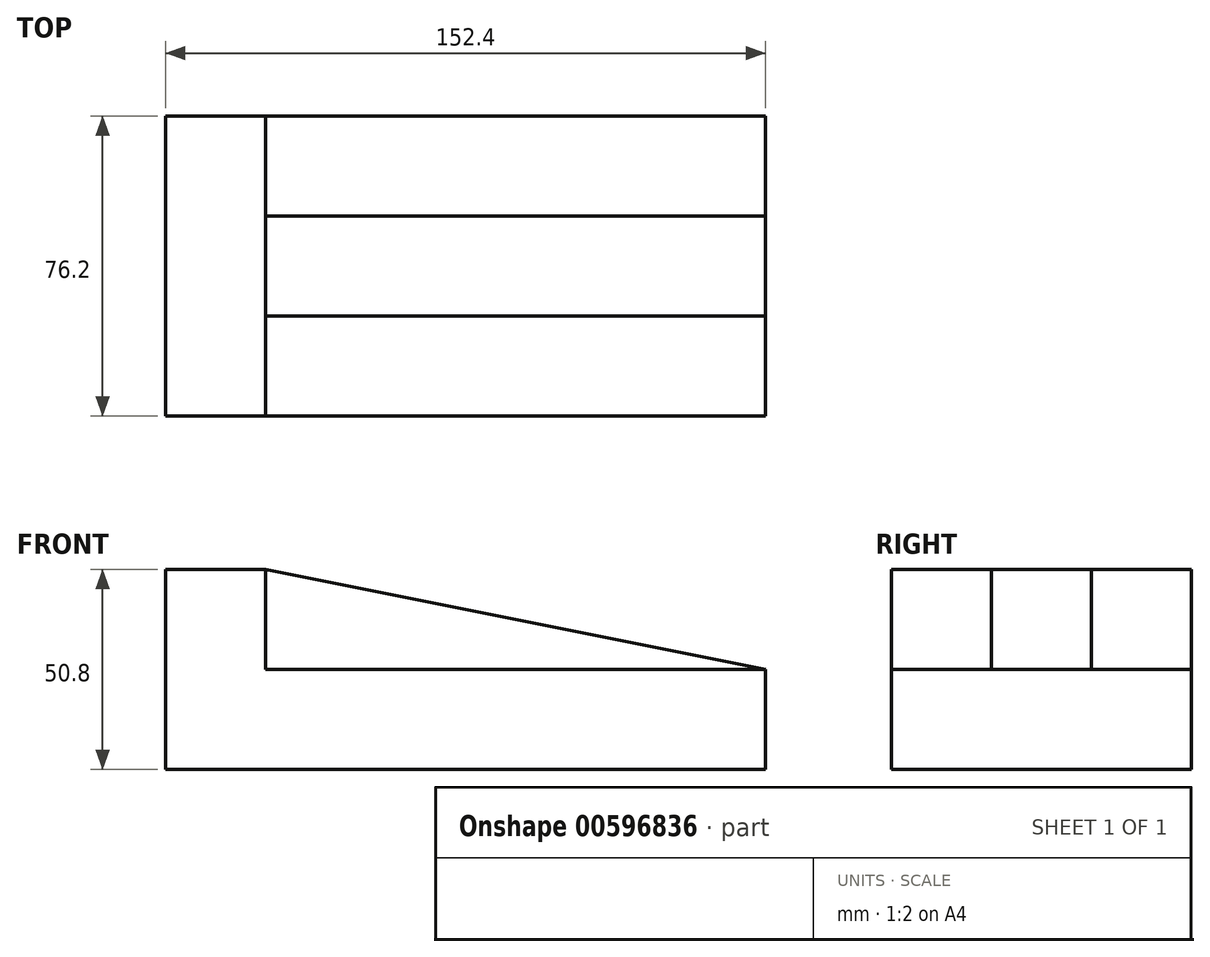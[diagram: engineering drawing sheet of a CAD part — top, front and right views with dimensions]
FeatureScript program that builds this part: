
annotation { "Feature Type Name" : "Feature", "Feature Type Description" : "" }
export const myFeature = defineFeature(function(context is Context, id is Id, definition is map)
    precondition{}
    {
        {
            var Q0;
            Q0=qCreatedBy(makeId("Front.planeOp"),FACE);
            var sketch = newSketch(context, id + "F0", { "sketchPlane" : qUnion([Q0])});
            skLineSegment(sketch, "E0", {"start": v(0, 0) * mm, "end": v(152.4, 0) * mm});
            skLineSegment(sketch, "E1", {"start": v(0, 0) * mm, "end": v(0, 50.8) * mm});
            skLineSegment(sketch, "E2", {"start": v(0, 50.8) * mm, "end": v(25.4, 50.8) * mm});
            skLineSegment(sketch, "E3", {"start": v(25.4, 50.8) * mm, "end": v(25.4, 25.4) * mm});
            skPoint(sketch, "E3.endSnap0", {"position": v(0, 25.4) * mm});
            skLineSegment(sketch, "E4", {"start": v(25.4, 25.4) * mm, "end": v(152.4, 25.4) * mm});
            skLineSegment(sketch, "E5", {"start": v(152.4, 25.4) * mm, "end": v(152.4, 0) * mm});
            skLineSegment(sketch, "E6", {"start": v(25.4, 50.8) * mm, "end": v(152.4, 25.4) * mm});
            skSolve(sketch);
        }
        {
            var Q0;
            Q0=makeQuery(id+"F0.imprint","IMPRINT",FACE,{"disambiguationData":[TD([[makeQuery(id+"F0.imprint","IMPRINT",EDGE,{"derivedFrom":sQuery(id+"F0.wireOp",EDGE,"E0")}),1.0]])]});
            extrude(context, id + "F1", {"entities" : qUnion([Q0]), "oppositeDirection" : true, "depth" : 76.2 * mm, "offsetDistance" : 25.4 * mm});
        }
        {
            var Q0;
            Q0=makeQuery(id+"F1.opExtrude","SWEPT_FACE",FACE,{"disambiguationData":[OSD([sQuery(id+"F0.wireOp",EDGE,"E3")])]});
            var sketch = newSketch(context, id + "F2", { "sketchPlane" : qUnion([Q0])});
            skLineSegment(sketch, "E7", {"start": v(0, 50.8) * mm, "end": v(25.4, 50.8) * mm});
            skLineSegment(sketch, "E8", {"start": v(25.4, 50.8) * mm, "end": v(25.4, 25.4) * mm});
            skLineSegment(sketch, "E9", {"start": v(76.2, 50.8) * mm, "end": v(50.8, 50.8) * mm});
            skLineSegment(sketch, "E10", {"start": v(50.8, 50.8) * mm, "end": v(50.8, 25.4) * mm});
            skSolve(sketch);
        }
        {
            var Q0;
            {var subQ0=sQuery(id+"F2.wireOp",EDGE,"E8");Q0=makeQuery(id+"F2.imprint","IMPRINT",FACE,{"disambiguationData":[TD([[makeQuery(id+"F2.imprint","IMPRINT",EDGE,{"derivedFrom":subQ0}),1.0]])]});}
            extrude(context, id + "F3", {"entities" : qUnion([Q0]), "operationType" : NewBodyOperationType.ADD, "depth" : 127 * mm, "offsetDistance" : 25.4 * mm});
        }
        {
            var Q0;
            Q0=makeQuery(id+"F3.opExtrude","SWEPT_FACE",FACE,{"disambiguationData":[OSD([sQuery(id+"F2.wireOp",EDGE,"E8")])]});
            var sketch = newSketch(context, id + "F4", { "sketchPlane" : qUnion([Q0])});
            skLineSegment(sketch, "E11", {"start": v(25.4, 50.8) * mm, "end": v(152.4, 25.4) * mm});
            skSolve(sketch);
        }
        {
            var Q0;
            Q0=makeQuery(id+"F4.imprint","IMPRINT",FACE,{"disambiguationData":[TD([[makeQuery(id+"F4.imprint","IMPRINT",EDGE,{"derivedFrom":sQuery(id+"F4.wireOp",EDGE,"E11")}),1.0]])]});
            extrude(context, id + "F5", {"entities" : qUnion([Q0]), "operationType" : NewBodyOperationType.REMOVE, "oppositeDirection" : true, "depth" : 25.4 * mm, "offsetDistance" : 25.4 * mm});
        }
    });
